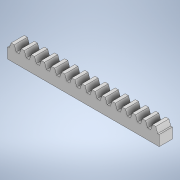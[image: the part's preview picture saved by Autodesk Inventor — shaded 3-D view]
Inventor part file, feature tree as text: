
AUTODESK INVENTOR PART (.ipt)
format: ipt  version: 2021 (Build 250183000, 183)  size: 158,208 bytes
history: native  units: mm
features: extrude x1, pattern_linear x1, sketch x1
ambient origin geometry x8: Origin, YZ Plane, XZ Plane, XY Plane, X Axis, Y Axis, Z Axis, Center Point
bodies: Solid1 (feature_tree)
feature tree (3):
  extrude  "Extrusion1"  Depth=2.0mm
  pattern_linear  "Rectangular Pattern1"  Spacing1=3.490659mm  [1 undecoded]
  sketch  "Sketch1"  dims[d0=1.2mm d1=2.0mm d2=3.490659mm d3=4.0mm d4=0.6mm d5=5.0mm d6=0.0mm d7=150.0mm d9=3.855mm]
note: 1 required parameter value undecoded (feature->parameter linkage not recoverable at this tier; creation-order binding heuristic only, values carry confidence <= 0.55)
